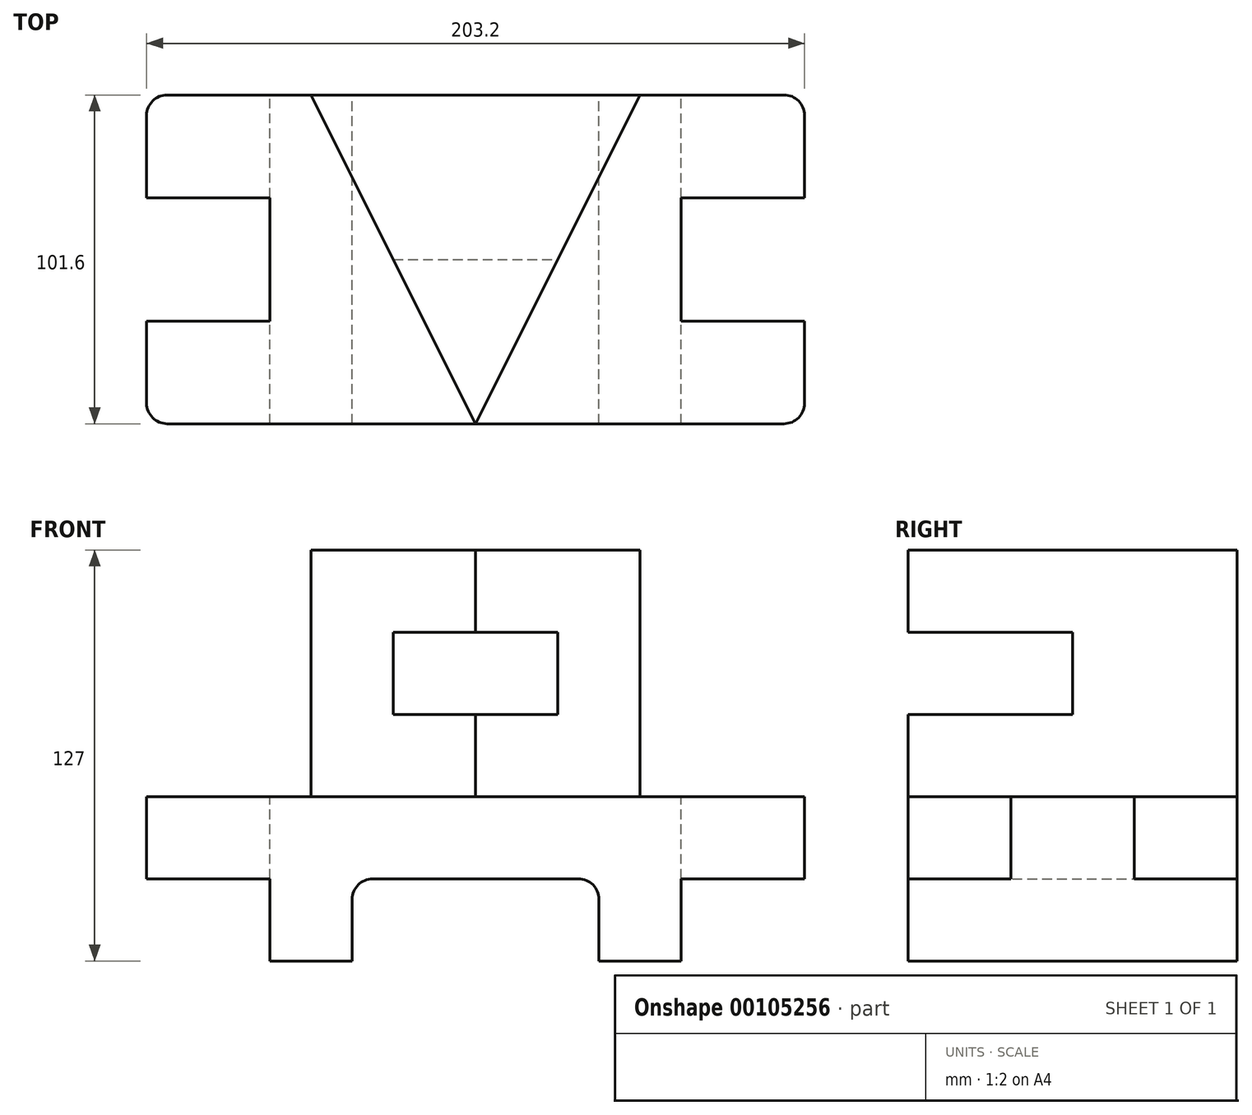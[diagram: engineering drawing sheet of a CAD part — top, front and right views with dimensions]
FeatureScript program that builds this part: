
annotation { "Feature Type Name" : "Feature", "Feature Type Description" : "" }
export const myFeature = defineFeature(function(context is Context, id is Id, definition is map)
    precondition{}
    {
        {
            var Q0;
            Q0=qCreatedBy(makeId("Front.planeOp"),FACE);
            var sketch = newSketch(context, id + "F0", { "sketchPlane" : qUnion([Q0])});
            skLineSegment(sketch, "E0", {"start": v(0, 0) * mm, "end": v(0, 25.4) * mm});
            skLineSegment(sketch, "E1", {"start": v(0, 25.4) * mm, "end": v(-38.1, 25.4) * mm});
            skLineSegment(sketch, "E2", {"start": v(-38.1, 25.4) * mm, "end": v(-38.1, 50.8) * mm});
            skLineSegment(sketch, "E3", {"start": v(-38.1, 50.8) * mm, "end": v(165.1, 50.8) * mm});
            skLineSegment(sketch, "E4", {"start": v(165.1, 50.8) * mm, "end": v(165.1, 25.4) * mm});
            skLineSegment(sketch, "E5", {"start": v(165.1, 25.4) * mm, "end": v(127, 25.4) * mm});
            skLineSegment(sketch, "E6", {"start": v(127, 25.4) * mm, "end": v(127, 0) * mm});
            skLineSegment(sketch, "E7", {"start": v(127, 0) * mm, "end": v(101.6, 0) * mm});
            skLineSegment(sketch, "E8", {"start": v(101.6, 0) * mm, "end": v(101.6, 25.4) * mm});
            skLineSegment(sketch, "E9", {"start": v(101.6, 25.4) * mm, "end": v(25.4, 25.4) * mm});
            skLineSegment(sketch, "E10", {"start": v(25.4, 25.4) * mm, "end": v(25.4, 0) * mm});
            skLineSegment(sketch, "E11", {"start": v(25.4, 0) * mm, "end": v(0, 0) * mm});
            skSolve(sketch);
        }
        {
            var Q0;
            Q0 = qSketchRegion(id + "F0", true);
            extrude(context, id + "F1", {"entities" : qUnion([Q0]), "endBound" : BoundingType.SYMMETRIC, "depth" : 101.6 * mm});
        }
        {
            var Q0;
            Q0=makeQuery(id+"F1.opExtrude","CAP_EDGE",EDGE,{"disambiguationData":[OSD([sQuery(id+"F0.wireOp",EDGE,"E2")])],"isStart":false});
            var Q1;
            Q1=makeQuery(id+"F1.opExtrude","CAP_EDGE",EDGE,{"disambiguationData":[OSD([sQuery(id+"F0.wireOp",EDGE,"E4")])],"isStart":false});
            var Q2;
            Q2=makeQuery(id+"F1.opExtrude","CAP_EDGE",EDGE,{"disambiguationData":[OSD([sQuery(id+"F0.wireOp",EDGE,"E4")])],"isStart":true});
            var Q3;
            Q3=makeQuery(id+"F1.opExtrude","CAP_EDGE",EDGE,{"disambiguationData":[OSD([sQuery(id+"F0.wireOp",EDGE,"E2")])],"isStart":true});
            fillet(context, id + "F2", {"entities" : qUnion([Q0, Q1, Q2, Q3]), "radius" : 6.35 * mm, "tangentPropagation" : true, "allowEdgeOverflow" : false});
        }
        {
            var Q0;
            Q0=makeQuery(id+"F1.opExtrude","SWEPT_FACE",FACE,{"disambiguationData":[OSD([sQuery(id+"F0.wireOp",EDGE,"E4")])]});
            var sketch = newSketch(context, id + "F3", { "sketchPlane" : qUnion([Q0])});
            skLineSegment(sketch, "E12.bottom", {"start": v(-19.05, 50.8) * mm, "end": v(19.05, 50.8) * mm});
            skLineSegment(sketch, "E12.top", {"start": v(-19.05, 25.4) * mm, "end": v(19.05, 25.4) * mm});
            skLineSegment(sketch, "E12.left", {"start": v(-19.05, 50.8) * mm, "end": v(-19.05, 25.4) * mm});
            skLineSegment(sketch, "E12.right", {"start": v(19.05, 50.8) * mm, "end": v(19.05, 25.4) * mm});
            skSolve(sketch);
        }
        {
            var Q0;
            Q0=makeQuery(id+"F3.imprint","IMPRINT",FACE,{"disambiguationData":[TD([[makeQuery(id+"F3.imprint","IMPRINT",EDGE,{"derivedFrom":sQuery(id+"F3.wireOp",EDGE,"E12.bottom")}),-1.0]])]});
            var Q1;
            Q1=makeQuery(id+"F1.opExtrude","SWEPT_FACE",FACE,{"disambiguationData":[OSD([sQuery(id+"F0.wireOp",EDGE,"E6")])]});
            extrude(context, id + "F4", {"entities" : qUnion([Q0]), "operationType" : NewBodyOperationType.REMOVE, "endBound" : BoundingType.UP_TO_SURFACE, "oppositeDirection" : true, "endBoundEntityFace" : qUnion([Q1]), "depth" : 25.4 * mm});
        }
        {
            var Q0;
            Q0=makeQuery(id+"F1.opExtrude","SWEPT_FACE",FACE,{"disambiguationData":[OSD([sQuery(id+"F0.wireOp",EDGE,"E2")])]});
            var sketch = newSketch(context, id + "F5", { "sketchPlane" : qUnion([Q0])});
            skLineSegment(sketch, "E13.bottom", {"start": v(-19.05, 50.8) * mm, "end": v(19.05, 50.8) * mm});
            skLineSegment(sketch, "E13.top", {"start": v(-19.05, 25.4) * mm, "end": v(19.05, 25.4) * mm});
            skLineSegment(sketch, "E13.left", {"start": v(-19.05, 50.8) * mm, "end": v(-19.05, 25.4) * mm});
            skLineSegment(sketch, "E13.right", {"start": v(19.05, 50.8) * mm, "end": v(19.05, 25.4) * mm});
            skSolve(sketch);
        }
        {
            var Q0;
            Q0=makeQuery(id+"F5.imprint","IMPRINT",FACE,{"disambiguationData":[TD([[makeQuery(id+"F5.imprint","IMPRINT",EDGE,{"derivedFrom":sQuery(id+"F5.wireOp",EDGE,"E13.bottom")}),1.0]])]});
            var Q1;
            Q1=makeQuery(id+"F1.opExtrude","SWEPT_FACE",FACE,{"disambiguationData":[OSD([sQuery(id+"F0.wireOp",EDGE,"E0")])]});
            extrude(context, id + "F6", {"entities" : qUnion([Q0]), "operationType" : NewBodyOperationType.REMOVE, "endBound" : BoundingType.UP_TO_SURFACE, "oppositeDirection" : true, "endBoundEntityFace" : qUnion([Q1]), "depth" : 25.4 * mm});
        }
        {
            var Q0;
            Q0=makeQuery(id+"F1.opExtrude","SWEPT_FACE",FACE,{"disambiguationData":[OSD([sQuery(id+"F0.wireOp",EDGE,"E3")])]});
            var sketch = newSketch(context, id + "F7", { "sketchPlane" : qUnion([Q0])});
            skLineSegment(sketch, "E14.bottom", {"start": v(12.7, 50.8) * mm, "end": v(114.3, 50.8) * mm});
            skLineSegment(sketch, "E14.top", {"start": v(12.7, -50.8) * mm, "end": v(114.3, -50.8) * mm});
            skLineSegment(sketch, "E14.left", {"start": v(12.7, 50.8) * mm, "end": v(12.7, -50.8) * mm});
            skLineSegment(sketch, "E14.right", {"start": v(114.3, 50.8) * mm, "end": v(114.3, -50.8) * mm});
            skSolve(sketch);
        }
        {
            var Q0;
            Q0 = qSketchRegion(id + "F7", true);
            extrude(context, id + "F8", {"entities" : qUnion([Q0]), "operationType" : NewBodyOperationType.ADD, "depth" : 76.2 * mm});
        }
        {
            var Q0;
            Q0=makeQuery(id+"F8.opExtrude","SWEPT_FACE",FACE,{"disambiguationData":[OSD([sQuery(id+"F7.wireOp",EDGE,"E14.right")])]});
            var sketch = newSketch(context, id + "F9", { "sketchPlane" : qUnion([Q0])});
            skLineSegment(sketch, "E15.bottom", {"start": v(-50.8, 101.6) * mm, "end": v(0, 101.6) * mm});
            skLineSegment(sketch, "E15.top", {"start": v(-50.8, 76.2) * mm, "end": v(0, 76.2) * mm});
            skLineSegment(sketch, "E15.left", {"start": v(-50.8, 101.6) * mm, "end": v(-50.8, 76.2) * mm});
            skLineSegment(sketch, "E15.right", {"start": v(0, 101.6) * mm, "end": v(0, 76.2) * mm});
            skSolve(sketch);
        }
        {
            var Q0;
            Q0=makeQuery(id+"F9.imprint","IMPRINT",FACE,{"disambiguationData":[TD([[makeQuery(id+"F9.imprint","IMPRINT",EDGE,{"derivedFrom":sQuery(id+"F9.wireOp",EDGE,"E15.bottom")}),-1.0]])]});
            extrude(context, id + "F10", {"entities" : qUnion([Q0]), "operationType" : NewBodyOperationType.REMOVE, "endBound" : BoundingType.THROUGH_ALL, "oppositeDirection" : true, "depth" : 25.4 * mm});
        }
        {
            var Q0;
            Q0=makeQuery(id+"F8.opExtrude","CAP_FACE",FACE,{"disambiguationData":[OSD([sQuery(id+"F7.wireOp",EDGE,"E14.bottom"),sQuery(id+"F7.wireOp",EDGE,"E14.top"),sQuery(id+"F7.wireOp",EDGE,"E14.left"),sQuery(id+"F7.wireOp",EDGE,"E14.right")])],"isStart":false});
            var sketch = newSketch(context, id + "F11", { "sketchPlane" : qUnion([Q0])});
            skLineSegment(sketch, "E16", {"start": v(12.7, 50.8) * mm, "end": v(63.5, -50.8) * mm});
            skSolve(sketch);
        }
        {
            var Q0;
            Q0 = qSketchRegion(id + "F11", true);
            var Q1;
            {var subQ0=sQuery(id+"F11.wireOp",EDGE,"E16");Q1=makeQuery(id+"F11.imprint","IMPRINT",FACE,{"disambiguationData":[TD([[makeQuery(id+"F11.imprint","IMPRINT",EDGE,{"derivedFrom":subQ0}),-1.0]])]});}
            var Q2;
            {var subQ0=sQuery(id+"F0.wireOp",EDGE,"E0");var subQ10=sQuery(id+"F0.wireOp",EDGE,"E3");Q2=makeQuery(id+"F8.boolean.opBoolean","SPLIT",FACE,{"disambiguationData":[TD([makeQuery(id+"F1.opExtrude","SWEPT_FACE",FACE,{"disambiguationData":[OSD([subQ0])]})])],"derivedFrom":makeQuery(id+"F1.opExtrude","SWEPT_FACE",FACE,{"disambiguationData":[OSD([subQ10])]})});}
            extrude(context, id + "F12", {"entities" : qUnion([Q0, Q1]), "operationType" : NewBodyOperationType.REMOVE, "endBound" : BoundingType.UP_TO_SURFACE, "oppositeDirection" : true, "endBoundEntityFace" : qUnion([Q2]), "depth" : 25.4 * mm});
        }
        {
            var Q0;
            Q0=makeQuery(id+"F8.opExtrude","CAP_FACE",FACE,{"disambiguationData":[OSD([sQuery(id+"F7.wireOp",EDGE,"E14.bottom"),sQuery(id+"F7.wireOp",EDGE,"E14.top"),sQuery(id+"F7.wireOp",EDGE,"E14.left"),sQuery(id+"F7.wireOp",EDGE,"E14.right")])],"isStart":false});
            var sketch = newSketch(context, id + "F13", { "sketchPlane" : qUnion([Q0])});
            skLineSegment(sketch, "E17", {"start": v(63.5, -50.8) * mm, "end": v(114.3, 50.8) * mm});
            skSolve(sketch);
        }
        {
            var Q0;
            Q0=makeQuery(id+"F13.imprint","IMPRINT",FACE,{"disambiguationData":[TD([[makeQuery(id+"F13.imprint","IMPRINT",EDGE,{"derivedFrom":sQuery(id+"F13.wireOp",EDGE,"E17")}),-1.0]])]});
            var Q1;
            {var subQ0=sQuery(id+"F0.wireOp",EDGE,"E4");var subQ8=sQuery(id+"F0.wireOp",EDGE,"E3");Q1=makeQuery(id+"F8.boolean.opBoolean","SPLIT",FACE,{"disambiguationData":[TD([makeQuery(id+"F1.opExtrude","SWEPT_FACE",FACE,{"disambiguationData":[OSD([subQ0])]})])],"derivedFrom":makeQuery(id+"F1.opExtrude","SWEPT_FACE",FACE,{"disambiguationData":[OSD([subQ8])]})});}
            extrude(context, id + "F14", {"entities" : qUnion([Q0]), "operationType" : NewBodyOperationType.REMOVE, "endBound" : BoundingType.UP_TO_SURFACE, "oppositeDirection" : true, "endBoundEntityFace" : qUnion([Q1]), "depth" : 25.4 * mm});
        }
        {
            var Q0;
            Q0=makeQuery(id+"F1.opExtrude","SWEPT_EDGE",EDGE,{"disambiguationData":[OSD([sQuery(id+"F0.wireOp",EDGE,"E9"),sQuery(id+"F0.wireOp",EDGE,"E10")])]});
            var Q1;
            Q1=makeQuery(id+"F1.opExtrude","SWEPT_EDGE",EDGE,{"disambiguationData":[OSD([sQuery(id+"F0.wireOp",EDGE,"E8"),sQuery(id+"F0.wireOp",EDGE,"E9")])]});
            fillet(context, id + "F15", {"entities" : qUnion([Q0, Q1]), "radius" : 6.35 * mm, "tangentPropagation" : true, "allowEdgeOverflow" : false});
        }
    });
